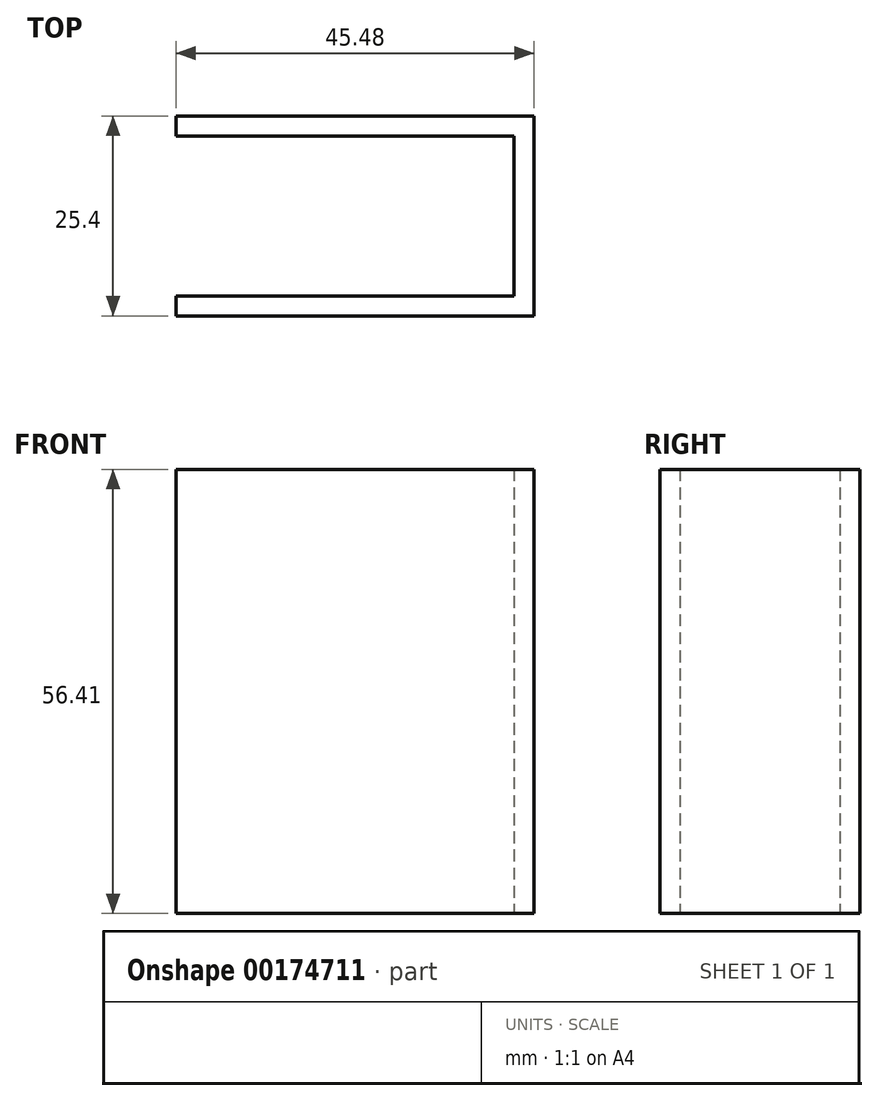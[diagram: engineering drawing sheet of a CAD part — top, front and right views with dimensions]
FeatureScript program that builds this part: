
annotation { "Feature Type Name" : "Feature", "Feature Type Description" : "" }
export const myFeature = defineFeature(function(context is Context, id is Id, definition is map)
    precondition{}
    {
        {
            var Q0;
            Q0=qCreatedBy(makeId("Front.planeOp"),FACE);
            var sketch = newSketch(context, id + "F0", { "sketchPlane" : qUnion([Q0])});
            skLineSegment(sketch, "E0.bottom", {"start": v(-59.58, 33.67) * mm, "end": v(-14.1, 33.67) * mm});
            skLineSegment(sketch, "E0.top", {"start": v(-59.58, -22.74) * mm, "end": v(-14.1, -22.74) * mm});
            skLineSegment(sketch, "E0.left", {"start": v(-59.58, 33.67) * mm, "end": v(-59.58, -22.74) * mm});
            skLineSegment(sketch, "E0.right", {"start": v(-14.1, 33.67) * mm, "end": v(-14.1, -22.74) * mm});
            skSolve(sketch);
        }
        {
            var Q0;
            Q0=makeQuery(id+"F0.imprint","IMPRINT",FACE,{"disambiguationData":[TD([[makeQuery(id+"F0.imprint","IMPRINT",EDGE,{"derivedFrom":sQuery(id+"F0.wireOp",EDGE,"E0.bottom")}),-1.0]])]});
            extrude(context, id + "F1", {"entities" : qUnion([Q0]), "depth" : 25.4 * mm});
        }
        {
            var Q0;
            Q0=makeQuery(id+"F1.opExtrude","SWEPT_FACE",FACE,{"disambiguationData":[OSD([sQuery(id+"F0.wireOp",EDGE,"E0.bottom")])]});
            var Q1;
            Q1=makeQuery(id+"F1.opExtrude","SWEPT_FACE",FACE,{"disambiguationData":[OSD([sQuery(id+"F0.wireOp",EDGE,"E0.left")])]});
            var Q2;
            Q2=makeQuery(id+"F1.opExtrude","SWEPT_FACE",FACE,{"disambiguationData":[OSD([sQuery(id+"F0.wireOp",EDGE,"E0.top")])]});
            shell(context, id + "F2", {"entities" : qUnion([Q0, Q1, Q2]), "thickness" : 2.54 * mm});
        }
    });
